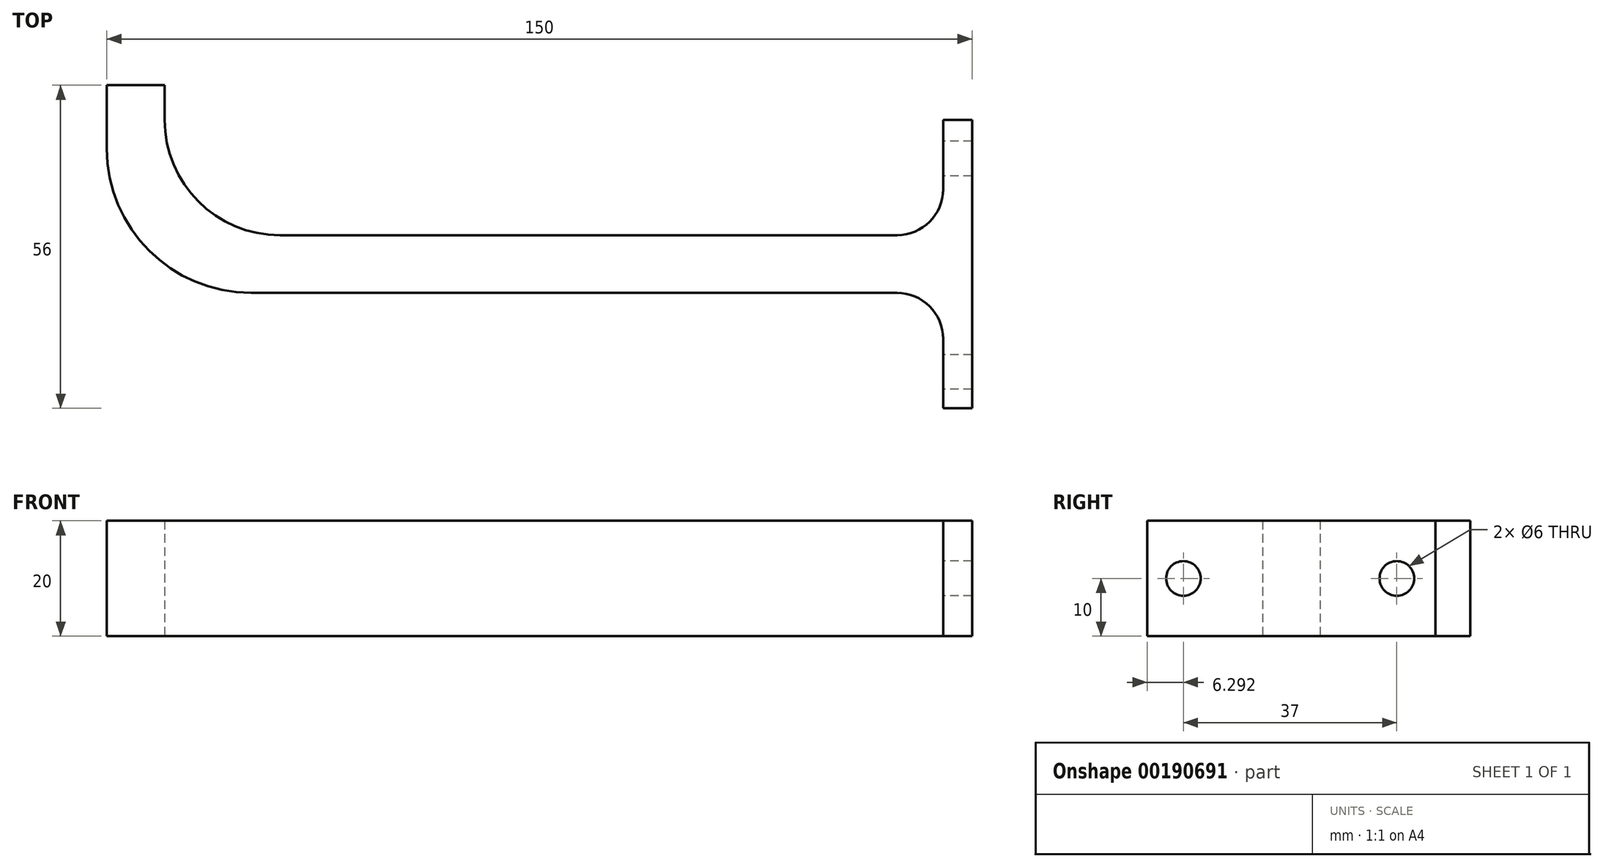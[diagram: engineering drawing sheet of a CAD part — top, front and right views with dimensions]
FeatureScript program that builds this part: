
annotation { "Feature Type Name" : "Feature", "Feature Type Description" : "" }
export const myFeature = defineFeature(function(context is Context, id is Id, definition is map)
    precondition{}
    {
        {
            var Q0;
            Q0=qCreatedBy(makeId("Top.planeOp"),FACE);
            var sketch = newSketch(context, id + "F0", { "sketchPlane" : qUnion([Q0])});
            skLineSegment(sketch, "E0", {"start": v(95.6, 16.1) * mm, "end": v(-39.4, 16.1) * mm});
            skLineSegment(sketch, "E1", {"start": v(-39.4, 16.1) * mm, "end": v(-39.4, 42.1) * mm});
            skLineSegment(sketch, "E2", {"start": v(-39.4, 42.1) * mm, "end": v(-49.4, 42.1) * mm});
            skLineSegment(sketch, "E3", {"start": v(-49.4, 42.1) * mm, "end": v(-49.4, 6.1) * mm});
            skLineSegment(sketch, "E4", {"start": v(-49.4, 6.1) * mm, "end": v(95.6, 6.1) * mm});
            skLineSegment(sketch, "E5", {"start": v(95.6, 6.1) * mm, "end": v(95.6, -13.9) * mm});
            skLineSegment(sketch, "E6", {"start": v(95.6, -13.9) * mm, "end": v(100.6, -13.9) * mm});
            skLineSegment(sketch, "E7", {"start": v(100.6, -13.9) * mm, "end": v(100.6, 16.1) * mm});
            skLineSegment(sketch, "E8", {"start": v(100.6, 16.1) * mm, "end": v(100.6, 36.1) * mm});
            skLineSegment(sketch, "E9", {"start": v(100.6, 36.1) * mm, "end": v(95.6, 36.1) * mm});
            skLineSegment(sketch, "E10", {"start": v(95.6, 36.1) * mm, "end": v(95.6, 16.1) * mm});
            skSolve(sketch);
        }
        {
            var Q0;
            Q0=makeQuery(id+"F0.imprint","IMPRINT",FACE,{"disambiguationData":[TD([[makeQuery(id+"F0.imprint","IMPRINT",EDGE,{"derivedFrom":sQuery(id+"F0.wireOp",EDGE,"E0")}),1.0]])]});
            extrude(context, id + "F1", {"entities" : qUnion([Q0]), "depth" : 20 * mm, "offsetDistance" : 25 * mm});
        }
        {
            var Q0;
            Q0=makeQuery(id+"F1.opExtrude","SWEPT_EDGE",EDGE,{"disambiguationData":[OSD([sQuery(id+"F0.wireOp",EDGE,"E3"),sQuery(id+"F0.wireOp",EDGE,"E4")])]});
            fillet(context, id + "F2", {"entities" : qUnion([Q0]), "radius" : 25 * mm, "tangentPropagation" : true, "allowEdgeOverflow" : false});
        }
        {
            var Q0;
            Q0=makeQuery(id+"F1.opExtrude","SWEPT_EDGE",EDGE,{"disambiguationData":[OSD([sQuery(id+"F0.wireOp",EDGE,"E4"),sQuery(id+"F0.wireOp",EDGE,"E5")])]});
            var Q1;
            Q1=makeQuery(id+"F1.opExtrude","SWEPT_EDGE",EDGE,{"disambiguationData":[OSD([sQuery(id+"F0.wireOp",EDGE,"E0"),sQuery(id+"F0.wireOp",EDGE,"E10")])]});
            fillet(context, id + "F3", {"entities" : qUnion([Q0, Q1]), "radius" : 8 * mm, "tangentPropagation" : true, "allowEdgeOverflow" : false});
        }
        {
            var Q0;
            Q0=makeQuery(id+"F1.opExtrude","SWEPT_FACE",FACE,{"disambiguationData":[OSD([sQuery(id+"F0.wireOp",EDGE,"E5")])]});
            var sketch = newSketch(context, id + "F4", { "sketchPlane" : qUnion([Q0])});
            skCircle(sketch, "E11", {"center": v(7.6, 10) * mm, "radius": 3 * mm});
            skPoint(sketch, "E11.centerSnap0", {"position": v(13.9, 10) * mm});
            skCircle(sketch, "E12", {"center": v(-29.4, 10) * mm, "radius": 3 * mm});
            skSolve(sketch);
        }
        {
            var Q0;
            Q0=makeQuery(id+"F4.imprint","IMPRINT",FACE,{"disambiguationData":[TD([[makeQuery(id+"F4.imprint","IMPRINT",EDGE,{"derivedFrom":sQuery(id+"F4.wireOp",EDGE,"E11")}),1.0]])]});
            var Q1;
            Q1=makeQuery(id+"F4.imprint","IMPRINT",FACE,{"disambiguationData":[TD([[makeQuery(id+"F4.imprint","IMPRINT",EDGE,{"derivedFrom":sQuery(id+"F4.wireOp",EDGE,"E12")}),1.0]])]});
            extrude(context, id + "F5", {"entities" : qUnion([Q0, Q1]), "operationType" : NewBodyOperationType.REMOVE, "oppositeDirection" : true, "depth" : 25 * mm, "offsetDistance" : 25 * mm});
        }
        {
            var Q0;
            Q0=makeQuery(id+"F1.opExtrude","SWEPT_EDGE",EDGE,{"disambiguationData":[OSD([sQuery(id+"F0.wireOp",EDGE,"E0"),sQuery(id+"F0.wireOp",EDGE,"E1")])]});
            fillet(context, id + "F6", {"entities" : qUnion([Q0]), "radius" : 20 * mm, "tangentPropagation" : true, "allowEdgeOverflow" : false});
        }
    });
